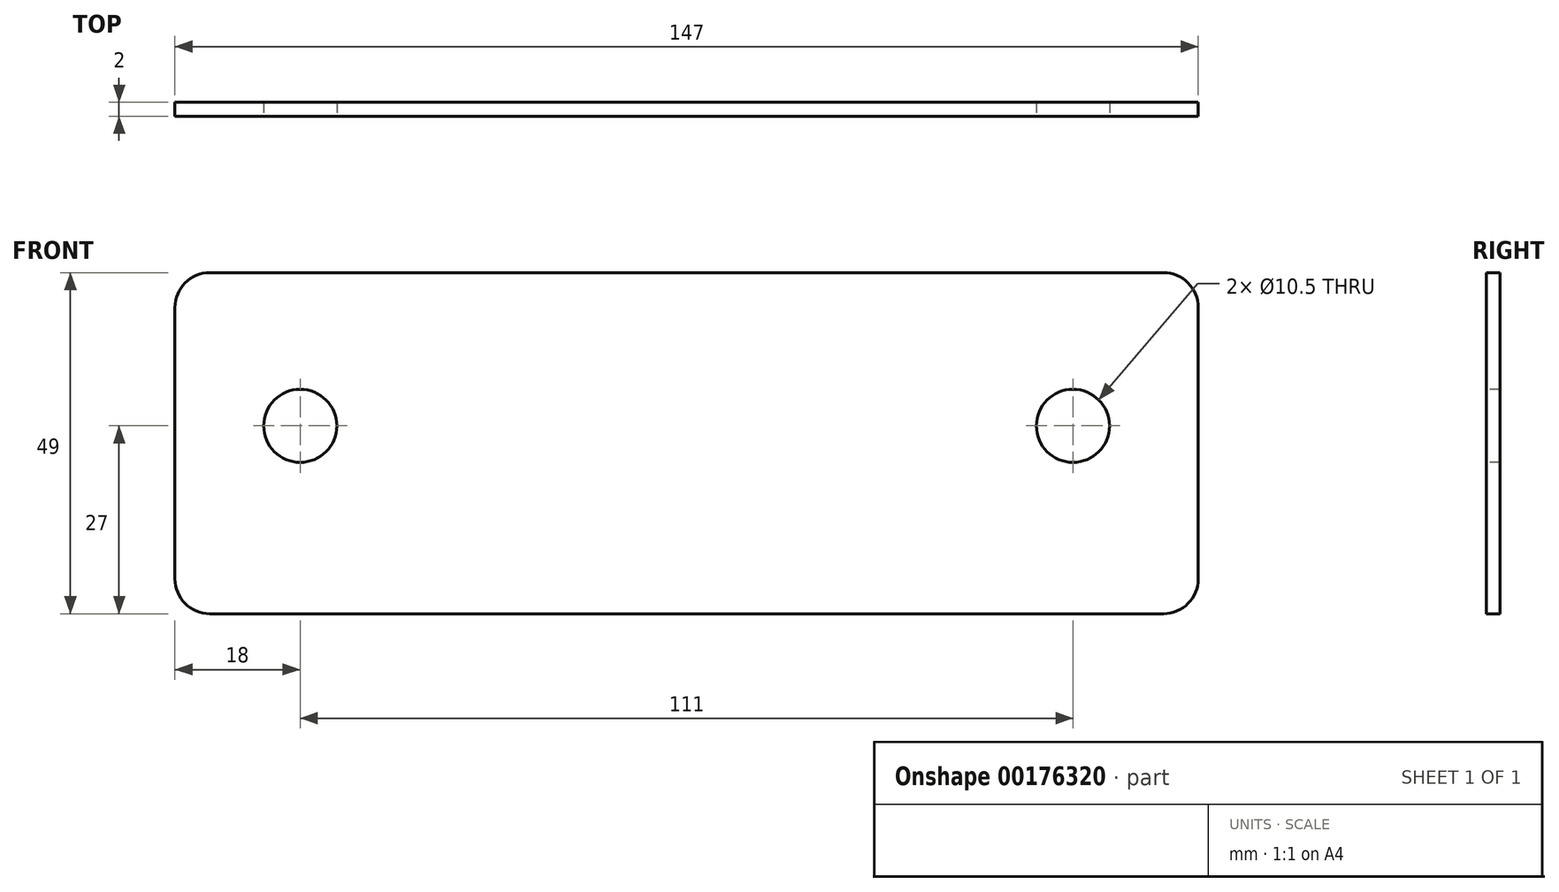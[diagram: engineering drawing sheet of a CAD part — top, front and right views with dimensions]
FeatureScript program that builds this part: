
annotation { "Feature Type Name" : "Feature", "Feature Type Description" : "" }
export const myFeature = defineFeature(function(context is Context, id is Id, definition is map)
    precondition{}
    {
        {
            var Q0;
            Q0=qCreatedBy(makeId("Front.planeOp"),FACE);
            var sketch = newSketch(context, id + "F0", { "sketchPlane" : qUnion([Q0])});
            skLineSegment(sketch, "E0", {"start": v(0, 0) * mm, "end": v(0, 49) * mm});
            skLineSegment(sketch, "E1", {"start": v(0, 49) * mm, "end": v(-147, 49) * mm});
            skLineSegment(sketch, "E2", {"start": v(-147, 49) * mm, "end": v(-147, 0) * mm});
            skLineSegment(sketch, "E3", {"start": v(-147, 0) * mm, "end": v(0, 0) * mm});
            skSolve(sketch);
        }
        {
            var Q0;
            Q0=makeQuery(id+"F0.imprint","IMPRINT",FACE,{"disambiguationData":[TD([[makeQuery(id+"F0.imprint","IMPRINT",EDGE,{"derivedFrom":sQuery(id+"F0.wireOp",EDGE,"E0")}),1.0]])]});
            extrude(context, id + "F1", {"entities" : qUnion([Q0]), "oppositeDirection" : true, "depth" : 2 * mm});
        }
        {
            var Q0;
            Q0=makeQuery(id+"F1.opExtrude","SWEPT_EDGE",EDGE,{"disambiguationData":[OSD([sQuery(id+"F0.wireOp",EDGE,"E0"),sQuery(id+"F0.wireOp",EDGE,"E1")])]});
            fillet(context, id + "F2", {"entities" : qUnion([Q0]), "radius" : 5 * mm, "tangentPropagation" : true, "allowEdgeOverflow" : false});
        }
        {
            var Q0;
            Q0=makeQuery(id+"F1.opExtrude","SWEPT_EDGE",EDGE,{"disambiguationData":[OSD([sQuery(id+"F0.wireOp",EDGE,"E0"),sQuery(id+"F0.wireOp",EDGE,"E3")])]});
            fillet(context, id + "F3", {"entities" : qUnion([Q0]), "radius" : 5 * mm, "tangentPropagation" : true, "allowEdgeOverflow" : false});
        }
        {
            var Q0;
            Q0=makeQuery(id+"F1.opExtrude","SWEPT_EDGE",EDGE,{"disambiguationData":[OSD([sQuery(id+"F0.wireOp",EDGE,"E2"),sQuery(id+"F0.wireOp",EDGE,"E3")])]});
            var Q1;
            Q1=makeQuery(id+"F1.opExtrude","SWEPT_EDGE",EDGE,{"disambiguationData":[OSD([sQuery(id+"F0.wireOp",EDGE,"E1"),sQuery(id+"F0.wireOp",EDGE,"E2")])]});
            fillet(context, id + "F4", {"entities" : qUnion([Q0, Q1]), "radius" : 5 * mm, "tangentPropagation" : true, "allowEdgeOverflow" : false});
        }
        {
            var Q0;
            Q0=makeQuery(id+"F1.opExtrude","CAP_FACE",FACE,{"disambiguationData":[OSD([sQuery(id+"F0.wireOp",EDGE,"E0"),sQuery(id+"F0.wireOp",EDGE,"E1"),sQuery(id+"F0.wireOp",EDGE,"E2"),sQuery(id+"F0.wireOp",EDGE,"E3")])],"isStart":true});
            var sketch = newSketch(context, id + "F5", { "sketchPlane" : qUnion([Q0])});
            skCircle(sketch, "E4", {"center": v(-18, 27) * mm, "radius": 5.25 * mm});
            skSolve(sketch);
        }
        {
            var Q0;
            Q0=makeQuery(id+"F5.imprint","IMPRINT",FACE,{"disambiguationData":[TD([[makeQuery(id+"F5.imprint","IMPRINT",EDGE,{"derivedFrom":sQuery(id+"F5.wireOp",EDGE,"E4")}),-1.0]])]});
            var sketch = newSketch(context, id + "F6", { "sketchPlane" : qUnion([Q0])});
            skCircle(sketch, "E5", {"center": v(-129, 27) * mm, "radius": 5.25 * mm});
            skSolve(sketch);
        }
        {
            var Q0;
            Q0=sQuery(id+"F6.wireOp",VERTEX,"E5.center");
            var Q1;
            Q1=sQuery(id+"F5.wireOp",VERTEX,"E4.center");
            var Q2;
            Q2=makeQuery(id+"F1.opExtrude","SWEPT_BODY",BODY,{"disambiguationData":[OSD([sQuery(id+"F0.wireOp",EDGE,"E0"),sQuery(id+"F0.wireOp",EDGE,"E1"),sQuery(id+"F0.wireOp",EDGE,"E2"),sQuery(id+"F0.wireOp",EDGE,"E3")])]});
            hole(context, id + "F7", {"style" : HoleStyle.SIMPLE, "endStyle" : HoleEndStyle.THROUGH, "holeDiameter" : 10.5 * mm, "locations" : qUnion([Q0, Q1]), "scope" : qUnion([Q2]), "isTappedThrough" : true});
        }
    });
